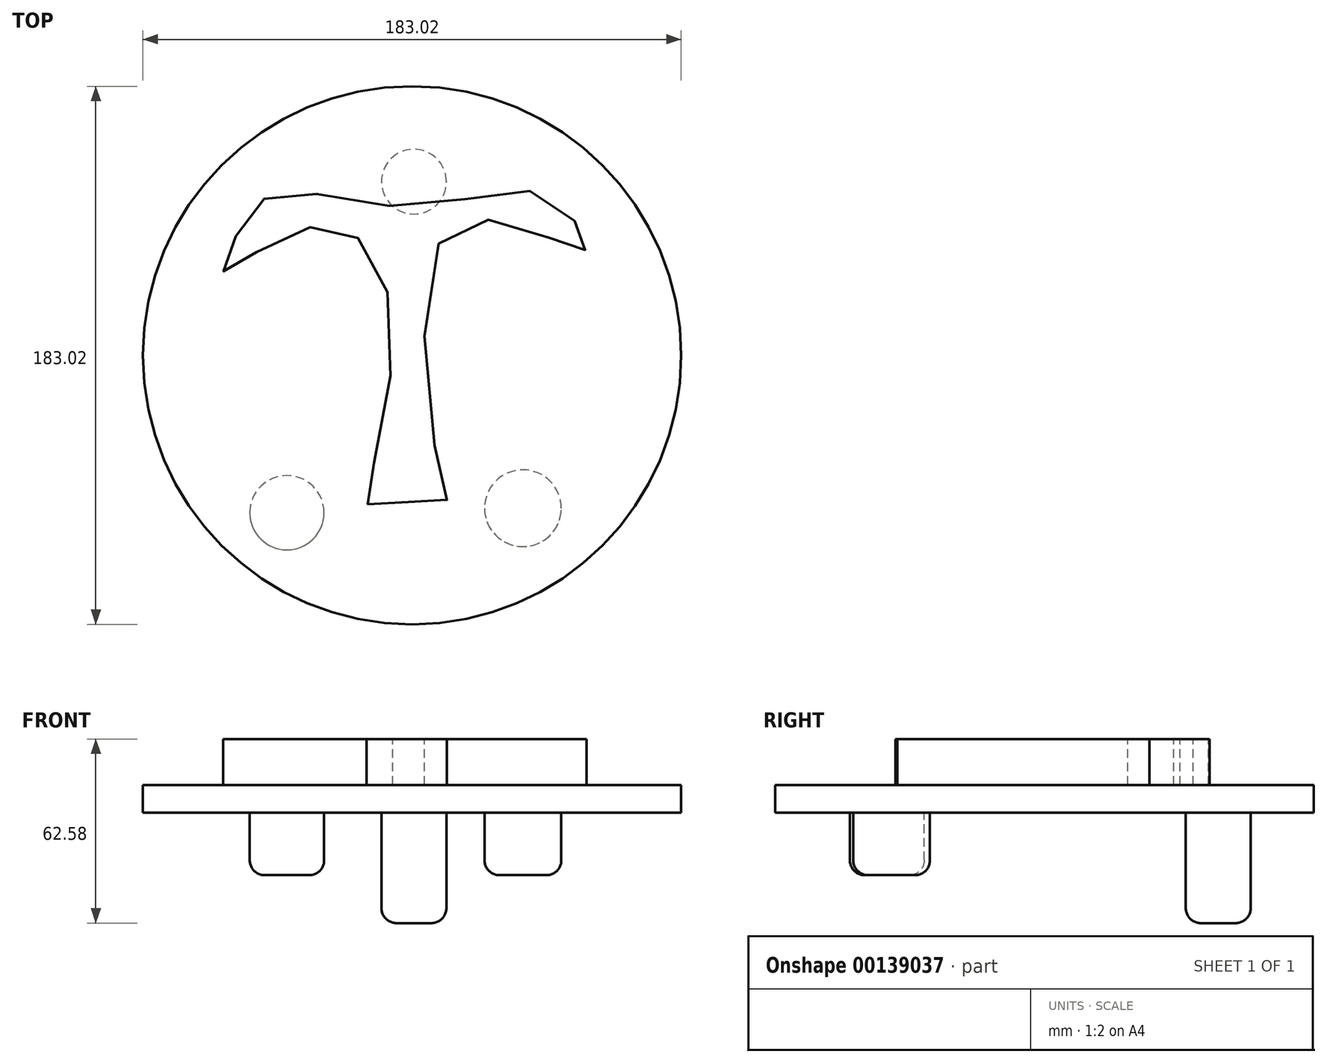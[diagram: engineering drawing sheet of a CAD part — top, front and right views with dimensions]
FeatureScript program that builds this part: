
annotation { "Feature Type Name" : "Feature", "Feature Type Description" : "" }
export const myFeature = defineFeature(function(context is Context, id is Id, definition is map)
    precondition{}
    {
        {
            var Q0;
            Q0=qCreatedBy(makeId("Top.planeOp"),FACE);
            var sketch = newSketch(context, id + "F0", { "sketchPlane" : qUnion([Q0])});
            skFitSpline(sketch, "E0", {"points": [v(-59.99, 40.55) * mm, v(-45.78, 55.18) * mm, v(0, 50.58) * mm, v(44.52, 54.76) * mm, v(59.15, 38.04) * mm, v(58.53, 35.74) * mm, v(37.62, 43.48) * mm, v(8.78, 37.41) * mm, v(11.08, -46.82) * mm, v(11.29, -49.75) * mm, v(-12.12, -50.17) * mm, v(-15.47, -50.17) * mm, v(-6.69, 0) * mm, v(-20.48, 41.39) * mm, v(-46.61, 39.09) * mm, v(-63.96, 28.43) * mm, v(-59.99, 40.55) * mm]});
            skSolve(sketch);
        }
        {
            var Q0;
            Q0=makeQuery(id+"F0.imprint","IMPRINT",FACE,{"disambiguationData":[TD([[makeQuery(id+"F0.imprint","IMPRINT",EDGE,{"derivedFrom":sQuery(id+"F0.wireOp",EDGE,"E0")}),-1.0]])]});
            extrude(context, id + "F1", {"entities" : qUnion([Q0]), "depth" : 10.53 * mm});
        }
        {
            var Q0;
            Q0=qCreatedBy(makeId("Top.planeOp"),FACE);
            var sketch = newSketch(context, id + "F2", { "sketchPlane" : qUnion([Q0])});
            skCircle(sketch, "E1", {"center": v(0, 0) * mm, "radius": 91.5 * mm});
            skSolve(sketch);
        }
        {
            var Q0;
            Q0=makeQuery(id+"F2.imprint","IMPRINT",FACE,{"disambiguationData":[TD([[makeQuery(id+"F2.imprint","IMPRINT",EDGE,{"derivedFrom":sQuery(id+"F2.wireOp",EDGE,"E1")}),1.0]])]});
            extrude(context, id + "F3", {"entities" : qUnion([Q0]), "operationType" : NewBodyOperationType.ADD, "oppositeDirection" : true, "depth" : 9.47 * mm});
        }
        {
            var Q0;
            Q0=makeQuery(id+"F1.opExtrude","CAP_FACE",FACE,{"disambiguationData":[OSD([sQuery(id+"F0.wireOp",EDGE,"E0")])],"isStart":false});
            extrude(context, id + "F4", {"entities" : qUnion([Q0]), "operationType" : NewBodyOperationType.ADD, "depth" : 5.07 * mm});
        }
        {
            var Q0;
            Q0=makeQuery(id+"F3.opExtrude","CAP_FACE",FACE,{"disambiguationData":[OSD([sQuery(id+"F2.wireOp",EDGE,"E1")])],"isStart":false});
            var sketch = newSketch(context, id + "F5", { "sketchPlane" : qUnion([Q0])});
            skCircle(sketch, "E2", {"center": v(0.63, -59.08) * mm, "radius": 11.04 * mm});
            skPoint(sketch, "E2.first.point", {"position": v(0, -48.06) * mm});
            skPoint(sketch, "E2.second.point", {"position": v(0, -70.1) * mm});
            skPoint(sketch, "E2.third.point", {"position": v(11.66, -59.1) * mm});
            skSolve(sketch);
        }
        {
            var Q0;
            Q0=makeQuery(id+"F5.imprint","IMPRINT",FACE,{"disambiguationData":[TD([[makeQuery(id+"F5.imprint","IMPRINT",EDGE,{"derivedFrom":sQuery(id+"F5.wireOp",EDGE,"E2")}),1.0]])]});
            extrude(context, id + "F6", {"entities" : qUnion([Q0]), "operationType" : NewBodyOperationType.ADD, "depth" : 37.52 * mm});
        }
        {
            var Q0;
            Q0=makeQuery(id+"F3.opExtrude","CAP_FACE",FACE,{"disambiguationData":[OSD([sQuery(id+"F2.wireOp",EDGE,"E1")])],"isStart":false});
            var sketch = newSketch(context, id + "F7", { "sketchPlane" : qUnion([Q0])});
            skCircle(sketch, "E3", {"center": v(37.68, 52) * mm, "radius": 13.04 * mm});
            skSolve(sketch);
        }
        {
            var Q0;
            Q0=makeQuery(id+"F7.imprint","IMPRINT",FACE,{"disambiguationData":[TD([[makeQuery(id+"F7.imprint","IMPRINT",EDGE,{"derivedFrom":sQuery(id+"F7.wireOp",EDGE,"E3")}),-1.0]])]});
            var sketch = newSketch(context, id + "F8", { "sketchPlane" : qUnion([Q0])});
            skCircle(sketch, "E4", {"center": v(-42.55, 53.53) * mm, "radius": 12.63 * mm});
            skSolve(sketch);
        }
        {
            var Q0;
            Q0=makeQuery(id+"F8.imprint","IMPRINT",FACE,{"disambiguationData":[TD([[makeQuery(id+"F8.imprint","IMPRINT",EDGE,{"derivedFrom":makeQuery(id+"F7.imprint","IMPRINT",EDGE,{"derivedFrom":sQuery(id+"F7.wireOp",EDGE,"E3")})}),1.0]])]});
            var Q1;
            Q1=makeQuery(id+"F8.imprint","IMPRINT",FACE,{"disambiguationData":[TD([[makeQuery(id+"F8.imprint","IMPRINT",EDGE,{"derivedFrom":sQuery(id+"F8.wireOp",EDGE,"E4")}),1.0]])]});
            extrude(context, id + "F9", {"entities" : qUnion([Q0, Q1]), "operationType" : NewBodyOperationType.ADD, "depth" : 21.24 * mm});
        }
        {
            var Q0;
            Q0=makeQuery(id+"F9.opExtrude","CAP_FACE",FACE,{"disambiguationData":[OSD([sQuery(id+"F7.wireOp",EDGE,"E3")])],"isStart":false});
            var Q1;
            Q1=makeQuery(id+"F9.opExtrude","CAP_FACE",FACE,{"disambiguationData":[OSD([sQuery(id+"F8.wireOp",EDGE,"E4")])],"isStart":false});
            fillet(context, id + "F10", {"entities" : qUnion([Q0, Q1]), "radius" : 5.08 * mm, "tangentPropagation" : true, "allowEdgeOverflow" : false});
        }
        {
            var Q0;
            Q0=makeQuery(id+"F6.opExtrude","CAP_FACE",FACE,{"disambiguationData":[OSD([sQuery(id+"F5.wireOp",EDGE,"E2")])],"isStart":false});
            fillet(context, id + "F11", {"entities" : qUnion([Q0]), "radius" : 5.08 * mm, "tangentPropagation" : true, "allowEdgeOverflow" : false});
        }
    });
